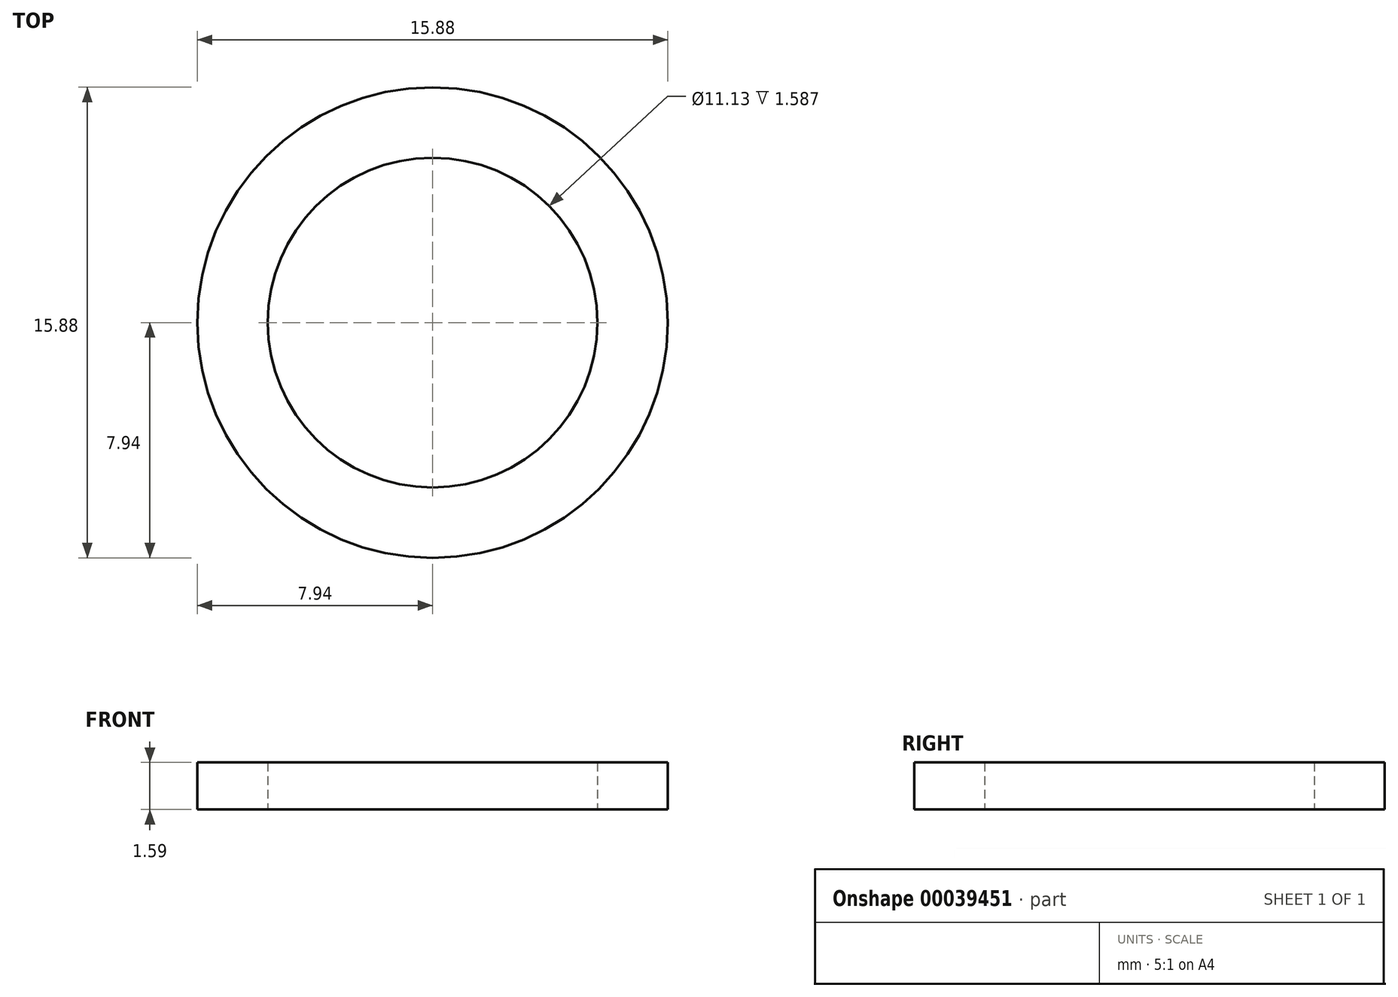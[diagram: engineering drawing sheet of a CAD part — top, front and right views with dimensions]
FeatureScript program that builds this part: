
annotation { "Feature Type Name" : "Feature", "Feature Type Description" : "" }
export const myFeature = defineFeature(function(context is Context, id is Id, definition is map)
    precondition{}
    {
        {
            var Q0;
            Q0=qCreatedBy(makeId("Top.planeOp"),FACE);
            var sketch = newSketch(context, id + "F0", { "sketchPlane" : qUnion([Q0])});
            skCircle(sketch, "E0", {"center": v(0, 0) * mm, "radius": 5.56 * mm});
            skCircle(sketch, "E1", {"center": v(0, 0) * mm, "radius": 7.94 * mm});
            skSolve(sketch);
        }
        {
            var Q0;
            Q0=makeQuery(id+"F0.imprint","IMPRINT",FACE,{"disambiguationData":[TD([[makeQuery(id+"F0.imprint","IMPRINT",EDGE,{"derivedFrom":sQuery(id+"F0.wireOp",EDGE,"E0")}),-1.0]])]});
            extrude(context, id + "F1", {"entities" : qUnion([Q0]), "depth" : 1.59 * mm});
        }
    });
